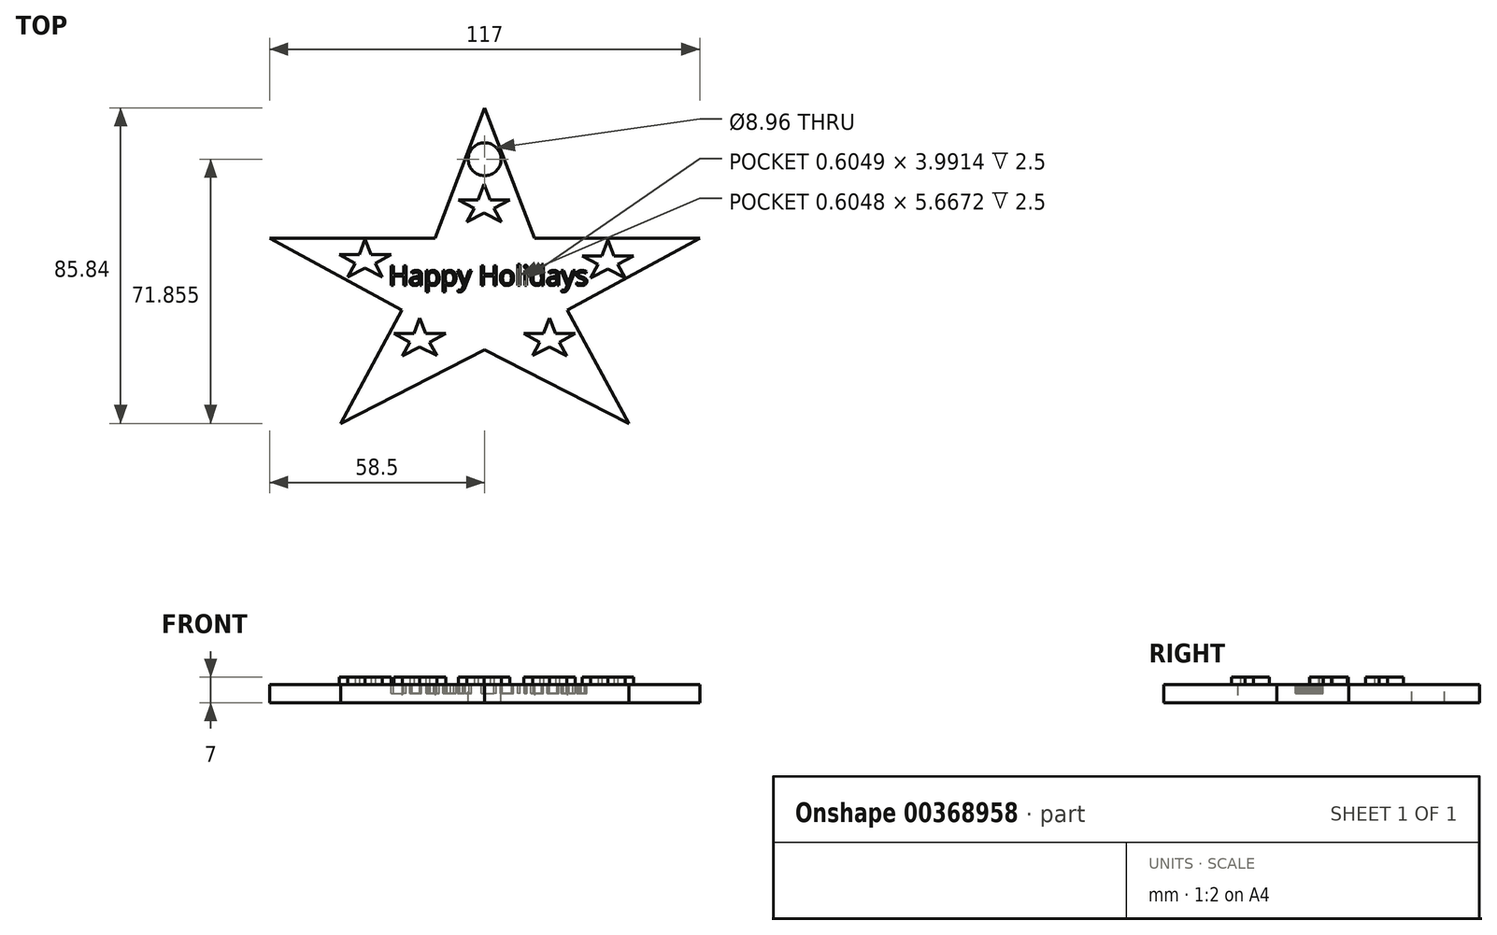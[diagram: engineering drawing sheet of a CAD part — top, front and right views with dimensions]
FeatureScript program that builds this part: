
annotation { "Feature Type Name" : "Feature", "Feature Type Description" : "" }
export const myFeature = defineFeature(function(context is Context, id is Id, definition is map)
    precondition{}
    {
        {
            var Q0;
            Q0=qCreatedBy(makeId("Top.planeOp"),FACE);
            var sketch = newSketch(context, id + "F0", { "sketchPlane" : qUnion([Q0])});
            skLineSegment(sketch, "E0", {"start": v(0, 55.08) * mm, "end": v(-13.5, 19.56) * mm});
            skLineSegment(sketch, "E1", {"start": v(-13.5, 19.56) * mm, "end": v(-58.5, 19.56) * mm});
            skLineSegment(sketch, "E2", {"start": v(-58.5, 19.56) * mm, "end": v(-22.47, 0) * mm});
            skLineSegment(sketch, "E3", {"start": v(-22.47, 0) * mm, "end": v(-39.17, -30.76) * mm});
            skLineSegment(sketch, "E4", {"start": v(-39.17, -30.76) * mm, "end": v(0, -10.71) * mm});
            skLineSegment(sketch, "E5", {"start": v(0, -10.71) * mm, "end": v(39.17, -30.76) * mm});
            skLineSegment(sketch, "E6", {"start": v(39.17, -30.76) * mm, "end": v(22.47, 0) * mm});
            skLineSegment(sketch, "E7", {"start": v(22.47, 0) * mm, "end": v(58.5, 19.56) * mm});
            skLineSegment(sketch, "E8", {"start": v(58.5, 19.56) * mm, "end": v(13.5, 19.56) * mm});
            skLineSegment(sketch, "E9", {"start": v(13.5, 19.56) * mm, "end": v(0, 55.08) * mm});
            skSolve(sketch);
        }
        {
            var Q0;
            Q0 = qSketchRegion(id + "F0", true);
            extrude(context, id + "F1", {"entities" : qUnion([Q0]), "depth" : 5 * mm});
        }
        {
            var Q0;
            Q0=makeQuery(id+"F1.opExtrude","CAP_FACE",FACE,{"disambiguationData":[OSD([sQuery(id+"F0.wireOp",EDGE,"E0"),sQuery(id+"F0.wireOp",EDGE,"E1"),sQuery(id+"F0.wireOp",EDGE,"E2"),sQuery(id+"F0.wireOp",EDGE,"E3"),sQuery(id+"F0.wireOp",EDGE,"E4"),sQuery(id+"F0.wireOp",EDGE,"E5"),sQuery(id+"F0.wireOp",EDGE,"E6"),sQuery(id+"F0.wireOp",EDGE,"E7"),sQuery(id+"F0.wireOp",EDGE,"E8"),sQuery(id+"F0.wireOp",EDGE,"E9")])],"isStart":false});
            var sketch = newSketch(context, id + "F2", { "sketchPlane" : qUnion([Q0])});
            skText(sketch, "E10", { "text": "Happy Holidays\n", "fontName": "OpenSans-Regular.ttf"});
            const initialGuessF2  = {"E10": [-0.02617, 0.0068, 1, 0, 0.00537]};
            skSetInitialGuess(sketch, initialGuessF2);
            skSolve(sketch);
        }
        {
            var Q0;
            Q0 = qSketchRegion(id + "F2", true);
            extrude(context, id + "F3", {"entities" : qUnion([Q0]), "operationType" : NewBodyOperationType.REMOVE, "oppositeDirection" : true, "depth" : 2.5 * mm});
        }
        {
            var Q0;
            {var subQ0=sQuery(id+"F0.wireOp",EDGE,"E8");var subQ1=sQuery(id+"F0.wireOp",EDGE,"E7");var subQ2=sQuery(id+"F0.wireOp",EDGE,"E6");var subQ3=sQuery(id+"F0.wireOp",EDGE,"E5");var subQ4=sQuery(id+"F0.wireOp",EDGE,"E4");var subQ5=sQuery(id+"F0.wireOp",EDGE,"E9");var subQ6=sQuery(id+"F0.wireOp",EDGE,"E0");var subQ7=sQuery(id+"F0.wireOp",EDGE,"E3");var subQ8=sQuery(id+"F0.wireOp",EDGE,"E1");var subQ9=sQuery(id+"F0.wireOp",EDGE,"E2");Q0=makeQuery(id+"F3.boolean.opBoolean","SPLIT",FACE,{"disambiguationData":[TD([makeQuery(id+"F1.opExtrude","SWEPT_FACE",FACE,{"disambiguationData":[OSD([subQ6])]})])],"derivedFrom":makeQuery(id+"F1.opExtrude","CAP_FACE",FACE,{"disambiguationData":[OSD([subQ6,subQ8,subQ9,subQ7,subQ4,subQ3,subQ2,subQ1,subQ0,subQ5])],"isStart":false})});}
            var sketch = newSketch(context, id + "F4", { "sketchPlane" : qUnion([Q0])});
            skCircle(sketch, "E11", {"center": v(0, 41.1) * mm, "radius": 4.48 * mm});
            skSolve(sketch);
        }
        {
            var Q0;
            Q0 = qSketchRegion(id + "F4", true);
            extrude(context, id + "F5", {"entities" : qUnion([Q0]), "operationType" : NewBodyOperationType.REMOVE, "oppositeDirection" : true, "depth" : 25 * mm});
        }
        {
            var Q0;
            Q0=qCreatedBy(makeId("Top.planeOp"),FACE);
            var sketch = newSketch(context, id + "F6", { "sketchPlane" : qUnion([Q0])});
            skLineSegment(sketch, "E12", {"start": v(-0.12, 34.35) * mm, "end": v(-1.74, 30.09) * mm});
            skLineSegment(sketch, "E13", {"start": v(-1.74, 30.09) * mm, "end": v(-7.15, 30.09) * mm});
            skLineSegment(sketch, "E14", {"start": v(-7.15, 30.09) * mm, "end": v(-2.82, 27.74) * mm});
            skLineSegment(sketch, "E15", {"start": v(-2.82, 27.74) * mm, "end": v(-4.83, 24.05) * mm});
            skLineSegment(sketch, "E16", {"start": v(-4.83, 24.05) * mm, "end": v(-0.12, 26.46) * mm});
            skLineSegment(sketch, "E17", {"start": v(-0.12, 26.46) * mm, "end": v(4.58, 24.05) * mm});
            skLineSegment(sketch, "E18", {"start": v(4.58, 24.05) * mm, "end": v(2.57, 27.74) * mm});
            skLineSegment(sketch, "E19", {"start": v(2.57, 27.74) * mm, "end": v(6.9, 30.09) * mm});
            skLineSegment(sketch, "E20", {"start": v(6.9, 30.09) * mm, "end": v(1.5, 30.09) * mm});
            skLineSegment(sketch, "E21", {"start": v(1.5, 30.09) * mm, "end": v(-0.12, 34.35) * mm});
            skLineSegment(sketch, "E22", {"start": v(-17.65, -2.05) * mm, "end": v(-19.27, -6.3) * mm});
            skLineSegment(sketch, "E23", {"start": v(-19.27, -6.3) * mm, "end": v(-24.67, -6.3) * mm});
            skLineSegment(sketch, "E24", {"start": v(-24.67, -6.3) * mm, "end": v(-20.34, -8.66) * mm});
            skLineSegment(sketch, "E25", {"start": v(-20.34, -8.66) * mm, "end": v(-22.35, -12.35) * mm});
            skLineSegment(sketch, "E26", {"start": v(-22.35, -12.35) * mm, "end": v(-17.65, -9.94) * mm});
            skLineSegment(sketch, "E27", {"start": v(-17.65, -9.94) * mm, "end": v(-13, -12.32) * mm});
            skLineSegment(sketch, "E28", {"start": v(-13, -12.32) * mm, "end": v(-14.98, -8.67) * mm});
            skLineSegment(sketch, "E29", {"start": v(-14.98, -8.67) * mm, "end": v(-10.62, -6.3) * mm});
            skLineSegment(sketch, "E30", {"start": v(-10.62, -6.3) * mm, "end": v(-16.02, -6.3) * mm});
            skLineSegment(sketch, "E31", {"start": v(-16.02, -6.3) * mm, "end": v(-17.65, -2.05) * mm});
            skLineSegment(sketch, "E32", {"start": v(17.65, -2.08) * mm, "end": v(16.02, -6.35) * mm});
            skLineSegment(sketch, "E33", {"start": v(16.02, -6.35) * mm, "end": v(10.62, -6.35) * mm});
            skLineSegment(sketch, "E34", {"start": v(10.62, -6.35) * mm, "end": v(14.95, -8.7) * mm});
            skLineSegment(sketch, "E35", {"start": v(14.95, -8.7) * mm, "end": v(13, -12.28) * mm});
            skLineSegment(sketch, "E36", {"start": v(13, -12.28) * mm, "end": v(17.57, -9.94) * mm});
            skLineSegment(sketch, "E37", {"start": v(17.57, -9.94) * mm, "end": v(22.35, -12.39) * mm});
            skLineSegment(sketch, "E38", {"start": v(22.35, -12.39) * mm, "end": v(20.34, -8.7) * mm});
            skLineSegment(sketch, "E39", {"start": v(20.34, -8.7) * mm, "end": v(24.67, -6.35) * mm});
            skLineSegment(sketch, "E40", {"start": v(24.67, -6.35) * mm, "end": v(19.27, -6.35) * mm});
            skLineSegment(sketch, "E41", {"start": v(19.27, -6.35) * mm, "end": v(17.65, -2.08) * mm});
            skLineSegment(sketch, "E42", {"start": v(33.5, 19.1) * mm, "end": v(31.88, 14.83) * mm});
            skLineSegment(sketch, "E43", {"start": v(31.88, 14.83) * mm, "end": v(26.48, 14.83) * mm});
            skLineSegment(sketch, "E44", {"start": v(26.48, 14.83) * mm, "end": v(30.8, 12.48) * mm});
            skLineSegment(sketch, "E45", {"start": v(30.8, 12.48) * mm, "end": v(28.8, 8.79) * mm});
            skLineSegment(sketch, "E46", {"start": v(28.8, 8.79) * mm, "end": v(33.5, 11.2) * mm});
            skLineSegment(sketch, "E47", {"start": v(33.5, 11.2) * mm, "end": v(38.2, 8.79) * mm});
            skLineSegment(sketch, "E48", {"start": v(38.2, 8.79) * mm, "end": v(36.2, 12.48) * mm});
            skLineSegment(sketch, "E49", {"start": v(36.2, 12.48) * mm, "end": v(40.52, 14.83) * mm});
            skLineSegment(sketch, "E50", {"start": v(40.52, 14.83) * mm, "end": v(35.12, 14.83) * mm});
            skLineSegment(sketch, "E51", {"start": v(35.12, 14.83) * mm, "end": v(33.5, 19.1) * mm});
            skLineSegment(sketch, "E52", {"start": v(-32.5, 19.4) * mm, "end": v(-34.12, 15.14) * mm});
            skLineSegment(sketch, "E53", {"start": v(-34.12, 15.14) * mm, "end": v(-39.53, 15.14) * mm});
            skLineSegment(sketch, "E54", {"start": v(-39.53, 15.14) * mm, "end": v(-35.2, 12.79) * mm});
            skLineSegment(sketch, "E55", {"start": v(-35.2, 12.79) * mm, "end": v(-37.2, 9.1) * mm});
            skLineSegment(sketch, "E56", {"start": v(-37.2, 9.1) * mm, "end": v(-32.5, 11.5) * mm});
            skLineSegment(sketch, "E57", {"start": v(-32.5, 11.5) * mm, "end": v(-27.8, 9.1) * mm});
            skLineSegment(sketch, "E58", {"start": v(-27.8, 9.1) * mm, "end": v(-29.8, 12.79) * mm});
            skLineSegment(sketch, "E59", {"start": v(-29.8, 12.79) * mm, "end": v(-25.48, 15.14) * mm});
            skLineSegment(sketch, "E60", {"start": v(-25.48, 15.14) * mm, "end": v(-30.88, 15.14) * mm});
            skLineSegment(sketch, "E61", {"start": v(-30.88, 15.14) * mm, "end": v(-32.5, 19.4) * mm});
            skSolve(sketch);
        }
        {
            var Q0;
            Q0 = qSketchRegion(id + "F6", true);
            extrude(context, id + "F7", {"entities" : qUnion([Q0]), "operationType" : NewBodyOperationType.ADD, "depth" : 7 * mm});
        }
    });
